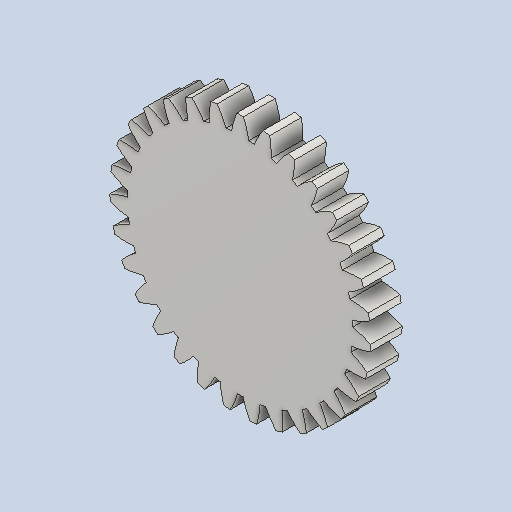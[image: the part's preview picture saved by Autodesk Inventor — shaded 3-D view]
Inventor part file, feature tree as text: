
AUTODESK INVENTOR PART (.ipt)
format: ipt  version: 2024 (Build 280153000, 153)  size: 270,848 bytes
history: native  units: mm (DEFAULTED — no unit token found)
features: plane x3, other x3, extrude x1, sketch x1
ambient origin geometry x8: Origin, YZ Plane, XZ Plane, XY Plane, X Axis, Y Axis, Z Axis, Center Point
bodies: Solid1 (feature_tree)
feature tree (8):
  extrude  "Extrusion1"  Depth=20.0mm TaperAngle=0.0deg
  plane  "Work Plane2"
  plane  "Work Plane8"
  plane  "Work Plane9"
  other  "Spur Gear"
  sketch  "Sketch1"  dims[d0=165.0mm d1=20.0mm d2=0.0mm d3=155.0mm d4=10.0mm d5=0.0mm d16=140.0mm d17=0.0mm d34=1.013417mm d39=0.0mm d41=0.0mm d43=140.0mm d46=140.0mm d47=0.0mm d48=0.0mm]
  other  "Srf1"
  other  "Pitch Diameter"
